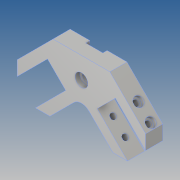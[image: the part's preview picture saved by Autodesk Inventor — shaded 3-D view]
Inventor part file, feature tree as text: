
AUTODESK INVENTOR PART (.ipt)
format: ipt  version: 2018.2 (Build 222227000, 227)  size: 184,320 bytes
history: native  units: mm
features: sketch x4, extrude x2, hole x2, mirror x2, plane x1
ambient origin geometry x8: Origin, YZ Plane, XZ Plane, XY Plane, X Axis, Y Axis, Z Axis, Center Point
bodies: Body1 (feature_tree)
feature tree (11):
  extrude  "Grundkörper"  Depth=30.0mm
  extrude  "NUT"  Depth=12.0mm
  hole  "DIN7984_M8_Bohrung"  [1 undecoded]
  plane  "Arbeitsebene_Bohrung"
  hole  "DIN7984_M6_Bohrung"  [1 undecoded]
  mirror  "DIN7984_M6_Bohrung_Spiegelung:1"
  mirror  "DIN7984_M6_Bohrung_Spiegelung:2"
  sketch  "Skizze1"  dims[d11=30.0mm d12=50.0mm]
  sketch  "Skizze2"  dims[d16=12.0mm d17=12.0mm]
  sketch  "Skizze4"  dims[d18=12.5mm d19=80.0mm]
  sketch  "Skizze5"  dims[d20=150.0mm d21=45.0deg d23=20.0mm d24=0.0mm d25=20.0mm d26=5.0mm d27=0.0mm d29=25.0mm d30=9.0mm d31=6.0mm d32=15.0mm d33=5.4mm d34=90.0deg d35=8.0mm d36=20.594885mm d37=20.0mm d39=18.0mm d40=6.6mm d41=6.0mm d42=11.0mm d43=4.4mm d44=90.0deg d45=8.0mm d46=20.594885mm]
note: 2 required parameter values undecoded (feature->parameter linkage not recoverable at this tier; creation-order binding heuristic only, values carry confidence <= 0.55)
